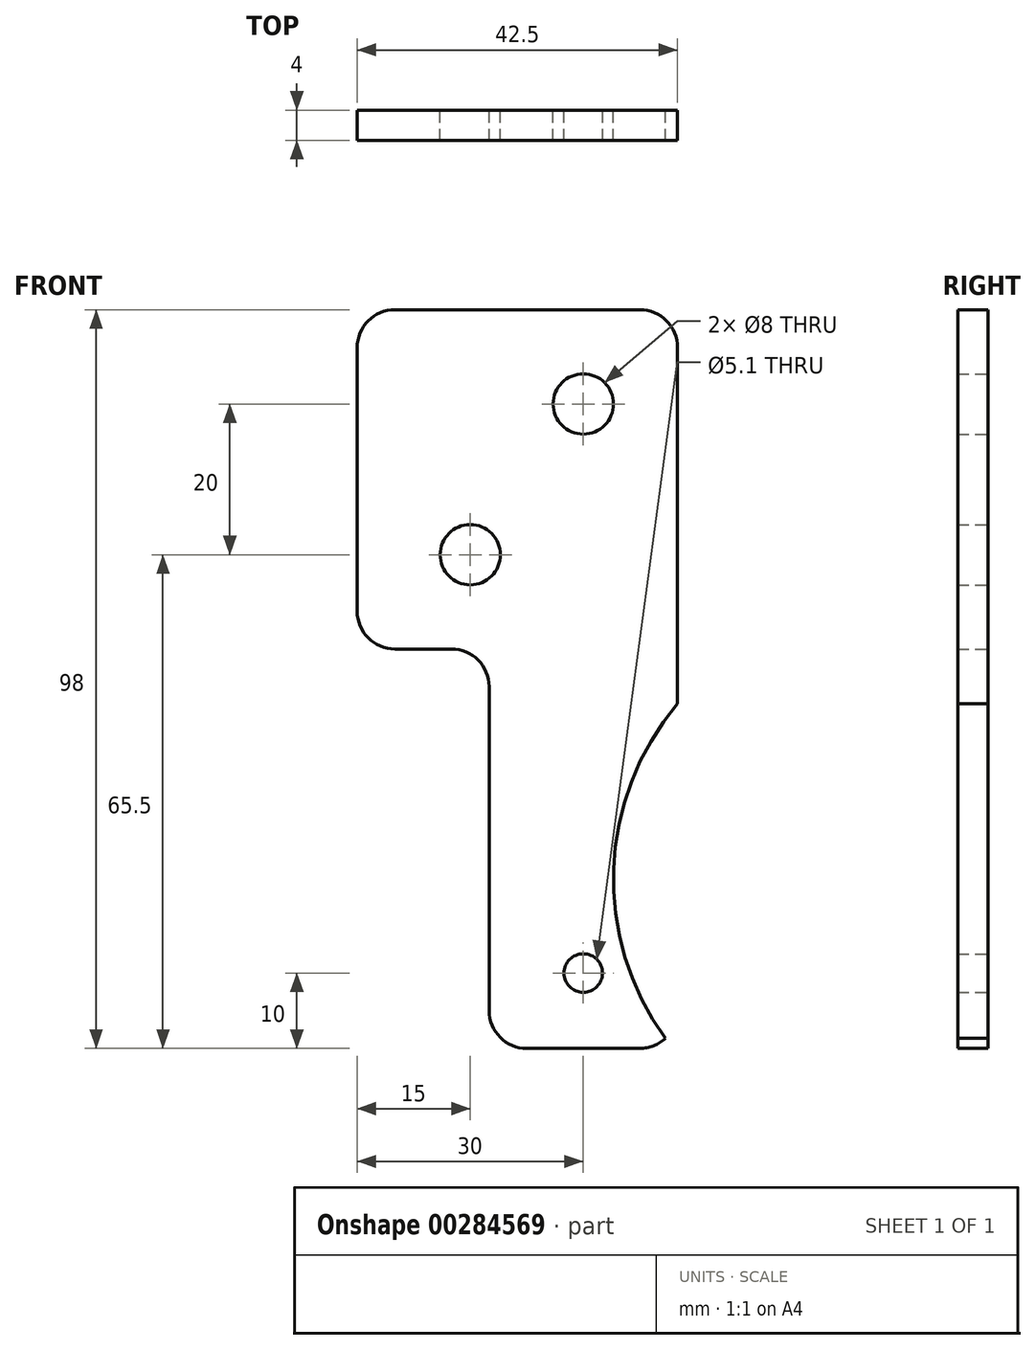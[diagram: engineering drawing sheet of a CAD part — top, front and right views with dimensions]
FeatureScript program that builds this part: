
annotation { "Feature Type Name" : "Feature", "Feature Type Description" : "" }
export const myFeature = defineFeature(function(context is Context, id is Id, definition is map)
    precondition{}
    {
        {
            var Q0;
            Q0=qCreatedBy(makeId("Front.planeOp"),FACE);
            var sketch = newSketch(context, id + "F0", { "sketchPlane" : qUnion([Q0])});
            skLineSegment(sketch, "E0", {"start": v(0, 5) * mm, "end": v(0, 48) * mm});
            skLineSegment(sketch, "E1", {"start": v(-5, 53) * mm, "end": v(-12.5, 53) * mm});
            skLineSegment(sketch, "E2", {"start": v(-17.5, 58) * mm, "end": v(-17.5, 93) * mm});
            skLineSegment(sketch, "E3", {"start": v(-12.5, 98) * mm, "end": v(20, 98) * mm});
            skLineSegment(sketch, "E4", {"start": v(25, 93) * mm, "end": v(25, 45.73) * mm});
            skLineSegment(sketch, "E5", {"start": v(20, 0) * mm, "end": v(5, 0) * mm});
            skPoint(sketch, "E6", {"position": v(12.5, 10) * mm});
            skPoint(sketch, "E7", {"position": v(12.5, 85.5) * mm});
            skPoint(sketch, "E8", {"position": v(-2.5, 65.5) * mm});
            skPoint(sketch, "E9.visualSharp", {"position": v(-17.5, 98) * mm});
            skArc(sketch, "E9.filletArc", {"start": v(-12.5, 98) * mm, "mid": v(-16.04, 96.54) * mm, "end": v(-17.5, 93) * mm});
            skPoint(sketch, "E10.visualSharp", {"position": v(25, 98) * mm});
            skArc(sketch, "E10.filletArc", {"start": v(25, 93) * mm, "mid": v(23.54, 96.54) * mm, "end": v(20, 98) * mm});
            skPoint(sketch, "E11.visualSharp", {"position": v(-17.5, 53) * mm});
            skArc(sketch, "E11.filletArc", {"start": v(-17.5, 58) * mm, "mid": v(-16.04, 54.46) * mm, "end": v(-12.5, 53) * mm});
            skPoint(sketch, "E12.visualSharp", {"position": v(0, 53) * mm});
            skArc(sketch, "E12.filletArc", {"start": v(0, 48) * mm, "mid": v(-1.46, 51.54) * mm, "end": v(-5, 53) * mm});
            skPoint(sketch, "E13.visualSharp", {"position": v(0, 0) * mm});
            skArc(sketch, "E13.filletArc", {"start": v(0, 5) * mm, "mid": v(1.46, 1.46) * mm, "end": v(5, 0) * mm});
            skPoint(sketch, "E14.visualSharp", {"position": v(25, 0) * mm});
            skArc(sketch, "E14.filletArc", {"start": v(20, 0) * mm, "mid": v(21.82, 0.34) * mm, "end": v(23.39, 1.32) * mm});
            skCircle(sketch, "E15", {"center": v(-2.5, 65.5) * mm, "radius": 4 * mm});
            skCircle(sketch, "E16", {"center": v(12.5, 85.5) * mm, "radius": 4 * mm});
            skCircle(sketch, "E17", {"center": v(12.5, 10) * mm, "radius": 2.55 * mm});
            skPoint(sketch, "E18", {"position": v(52.5, 22.5) * mm});
            skArc(sketch, "E19", {"start": v(25, 45.73) * mm, "mid": v(16.52, 23.8) * mm, "end": v(23.39, 1.32) * mm});
            skSolve(sketch);
        }
        {
            var Q0;
            Q0 = qSketchRegion(id + "F0", true);
            extrude(context, id + "F1", {"entities" : qUnion([Q0]), "depth" : 4 * mm});
        }
    });
